# Revit family: ledspot3c-p_30w-3000-40d-bl_140054443
name_source: partatom
category: Leuchten
revit_build: Autodesk Revit 2016 (Build: 20190508_0715(x64)
units: mm (PartAtom-declared; Revit-internal decimal feet)

## family parameters
Basisbauteil = Fläche
Beim Laden mit Abzugskörper schneiden = Nein
Bemaßung runder Anschluss = Durchmesser verwenden
Gemeinsam genutzt = Nein
Lichtquelle = Nein
Raumberechnungspunkt = Nein
Teiletyp = Normal

## types (1)
- LEDSpot3C-P 30W-3000-40D-BL (1 x LED, 2400 lm)
    Approval mark = CE, ENEC
    Beschreibung = Powerful track spot with attractive design with classic cylinder and box shapes that easily fits into shop architectures. Fitting common Global/Nordic Aluminum® 3C Tracks – and many other standard types. Low glare due to matte black anti-glare ring.
    CIE Flux Codes = 94 99 100 100 100
    Control Gear = Electronic ballast
    Height = 175 mm
    Hersteller = OPPLE
    Lamp Light Flux = 2400 lm
    Lamp count = 1
    Lampe = 1 x LED
    Length = 155 mm
    Luminous efficacy = 77 lm/W
    ModVariant = Nein
    Modell = 140054443
    Mounting Place = Ceiling
    Mounting Type = Surface mounted
    Number of Poles = 1
    OnlyDefault = Ja
    Power Factor = 1
    Product Name = LEDSpot3C-P 30W-3000-40D-BL
    Product group = Spot Performer 3C
    ProductGroupID = 330
    Protection Class = Protection class I
    Protection Degree = IP 20
    RLX_Detail_Level = 1
    RlxData = <blob elided: 128333 chars, md5=64621278>
    Scheinlast = 31 VA
    Socket = socket
    Standby Power = 0 W
    System Light Flux = 2400 lm
    System Power = 31 W
    Typenbild = 140054443.jpg
    Typenkommentare = Product without accessories
    URL = http://relux.com
    VarID = ---
    Voltage = 0 V
    Vorgabe-Ansicht = 1800 mm
    Weight = 0.00 kg
    Width = 90 mm

## geometry (parser evidence)
native form markers: Blend x4, Sweep x13
no freeform markers — native parametric forms only
